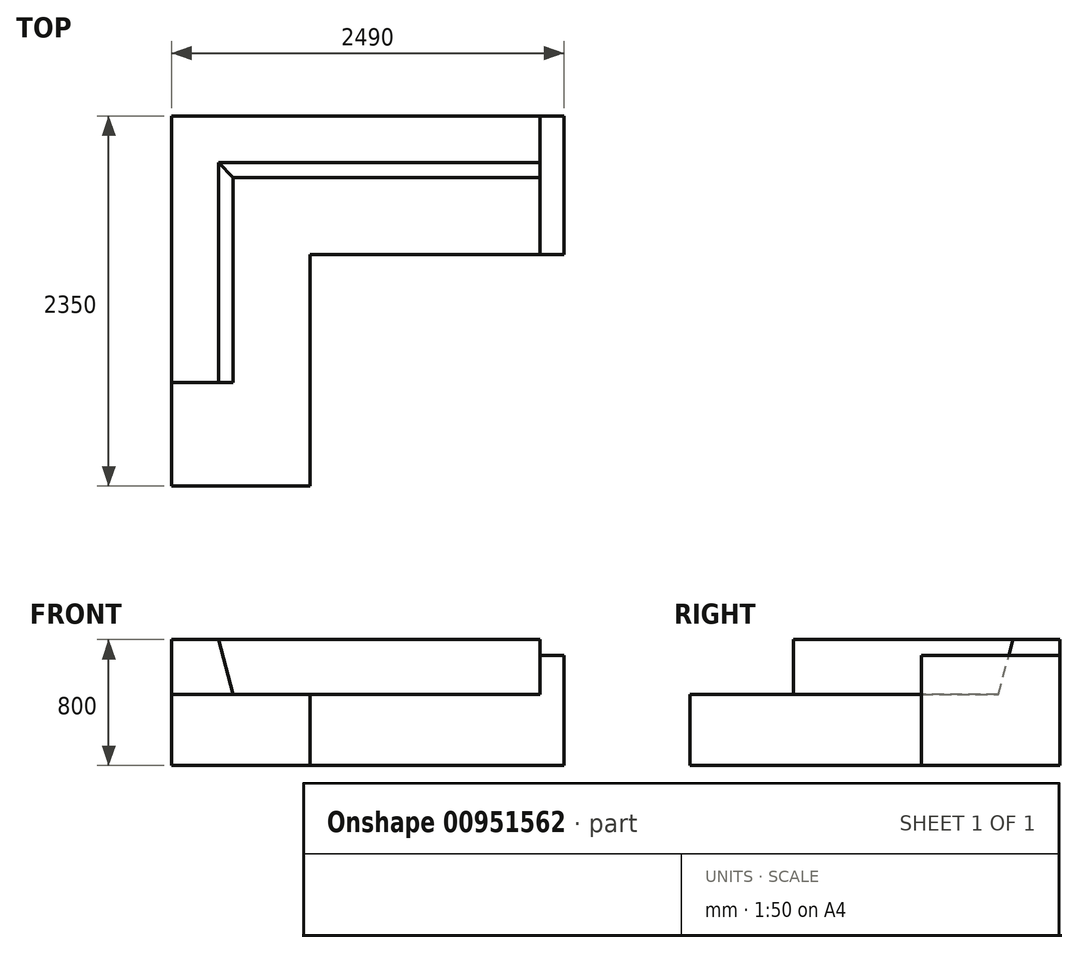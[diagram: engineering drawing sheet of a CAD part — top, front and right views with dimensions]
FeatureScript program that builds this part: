
annotation { "Feature Type Name" : "Feature", "Feature Type Description" : "" }
export const myFeature = defineFeature(function(context is Context, id is Id, definition is map)
    precondition{}
    {
        {
            var Q0;
            Q0=qCreatedBy(makeId("Top.planeOp"),FACE);
            var sketch = newSketch(context, id + "F0", { "sketchPlane" : qUnion([Q0])});
            skLineSegment(sketch, "E0", {"start": v(0, 0) * mm, "end": v(0, 2350) * mm});
            skLineSegment(sketch, "E1", {"start": v(0, 2350) * mm, "end": v(2490, 2350) * mm});
            skLineSegment(sketch, "E2", {"start": v(0, 0) * mm, "end": v(879.48, 0) * mm});
            skLineSegment(sketch, "E3", {"start": v(2490, 2350) * mm, "end": v(2490, 1470.52) * mm});
            skLineSegment(sketch, "E4", {"start": v(879.48, 0) * mm, "end": v(879.48, 1470.52) * mm});
            skLineSegment(sketch, "E5", {"start": v(879.48, 1470.52) * mm, "end": v(2490, 1470.52) * mm});
            skSolve(sketch);
        }
        {
            var Q0;
            Q0=qSketchRegion(id+"F0",true);
            extrude(context, id + "F1", {"entities" : qUnion([Q0]), "depth" : 450 * mm, "offsetDistance" : 25.4 * mm});
        }
        {
            var Q0;
            Q0=makeQuery(id+"F1.opExtrude","CAP_FACE",FACE,{"disambiguationData":[OSD([sQuery(id+"F0.wireOp",EDGE,"E0"),sQuery(id+"F0.wireOp",EDGE,"E1"),sQuery(id+"F0.wireOp",EDGE,"E2"),sQuery(id+"F0.wireOp",EDGE,"E3"),sQuery(id+"F0.wireOp",EDGE,"E4"),sQuery(id+"F0.wireOp",EDGE,"E5")])],"isStart":false});
            var sketch = newSketch(context, id + "F2", { "sketchPlane" : qUnion([Q0])});
            skLineSegment(sketch, "E6.bottom", {"start": v(879.48, 0) * mm, "end": v(0, 0) * mm});
            skLineSegment(sketch, "E6.top", {"start": v(879.48, 150) * mm, "end": v(0, 150) * mm});
            skLineSegment(sketch, "E6.left", {"start": v(879.48, 0) * mm, "end": v(879.48, 150) * mm});
            skLineSegment(sketch, "E6.right", {"start": v(0, 0) * mm, "end": v(0, 150) * mm});
            skLineSegment(sketch, "E7.bottom", {"start": v(2490, 1470.52) * mm, "end": v(2340, 1470.52) * mm});
            skLineSegment(sketch, "E7.top", {"start": v(2490, 2350) * mm, "end": v(2340, 2350) * mm});
            skLineSegment(sketch, "E7.left", {"start": v(2490, 1470.52) * mm, "end": v(2490, 2350) * mm});
            skLineSegment(sketch, "E7.right", {"start": v(2340, 1470.52) * mm, "end": v(2340, 2350) * mm});
            skSolve(sketch);
        }
        {
            var Q0;
            Q0=qSketchRegion(id+"F2",true);
            extrude(context, id + "F3", {"entities" : qUnion([Q0]), "operationType" : NewBodyOperationType.ADD, "depth" : 700 * mm - 450 * mm, "offsetDistance" : 25.4 * mm});
        }
        {
            var Q0;
            Q0=makeQuery(id+"F3.opExtrude","SWEPT_FACE",FACE,{"disambiguationData":[OSD([sQuery(id+"F2.wireOp",EDGE,"E6.top")])]});
            var sketch = newSketch(context, id + "F4", { "sketchPlane" : qUnion([Q0])});
            skLineSegment(sketch, "E8", {"start": v(0, 450) * mm, "end": v(0, 800) * mm});
            skLineSegment(sketch, "E9", {"start": v(0, 800) * mm, "end": v(-296.74, 800) * mm});
            skLineSegment(sketch, "E10", {"start": v(-296.74, 800) * mm, "end": v(-390.52, 450) * mm});
            skLineSegment(sketch, "E11", {"start": v(-390.52, 450) * mm, "end": v(0, 450) * mm});
            skSolve(sketch);
        }
        {
            var Q0;
            Q0=qSketchRegion(id+"F4",true);
            var Q1;
            Q1=makeQuery(id+"F3.boolean.opBoolean","MERGE",FACE,{"derivedFrom":[makeQuery(id+"F1.opExtrude","SWEPT_FACE",FACE,{"disambiguationData":[OSD([sQuery(id+"F0.wireOp",EDGE,"E1")])]}),makeQuery(id+"F3.opExtrude","SWEPT_FACE",FACE,{"disambiguationData":[OSD([sQuery(id+"F2.wireOp",EDGE,"E7.top")])]})]});
            extrude(context, id + "F5", {"entities" : qUnion([Q0]), "operationType" : NewBodyOperationType.ADD, "endBound" : BoundingType.UP_TO_SURFACE, "depth" : 25.4 * mm, "endBoundEntityFace" : qUnion([Q1]), "offsetDistance" : 25.4 * mm});
        }
        {
            var Q0;
            Q0=makeQuery(id+"F3.opExtrude","SWEPT_FACE",FACE,{"disambiguationData":[OSD([sQuery(id+"F2.wireOp",EDGE,"E7.right")])]});
            var sketch = newSketch(context, id + "F6", { "sketchPlane" : qUnion([Q0])});
            skLineSegment(sketch, "E12", {"start": v(-2350, 450) * mm, "end": v(-1959.47, 450) * mm});
            skLineSegment(sketch, "E13", {"start": v(-1959.47, 450) * mm, "end": v(-2053.26, 800) * mm});
            skLineSegment(sketch, "E14", {"start": v(-2053.26, 800) * mm, "end": v(-2350, 800) * mm});
            skLineSegment(sketch, "E15", {"start": v(-2350, 800) * mm, "end": v(-2350, 450) * mm});
            skSolve(sketch);
        }
        {
            var Q0;
            Q0=qSketchRegion(id+"F6",true);
            extrude(context, id + "F7", {"entities" : qUnion([Q0]), "operationType" : NewBodyOperationType.ADD, "endBound" : BoundingType.UP_TO_NEXT, "depth" : 25.4 * mm, "offsetDistance" : 25.4 * mm});
        }
        {
            var Q0;
            Q0=makeQuery(id+"F3.boolean.opBoolean","MERGE",FACE,{"derivedFrom":[makeQuery(id+"F1.opExtrude","SWEPT_FACE",FACE,{"disambiguationData":[OSD([sQuery(id+"F0.wireOp",EDGE,"E4")])]}),makeQuery(id+"F3.opExtrude","SWEPT_FACE",FACE,{"disambiguationData":[OSD([sQuery(id+"F2.wireOp",EDGE,"E6.left")])]})]});
            var sketch = newSketch(context, id + "F8", { "sketchPlane" : qUnion([Q0])});
            skLineSegment(sketch, "E16.bottom", {"start": v(658.57, 450) * mm, "end": v(0, 450) * mm});
            skLineSegment(sketch, "E16.top", {"start": v(658.57, 800) * mm, "end": v(0, 800) * mm});
            skLineSegment(sketch, "E16.left", {"start": v(658.57, 450) * mm, "end": v(658.57, 800) * mm});
            skLineSegment(sketch, "E16.right", {"start": v(0, 450) * mm, "end": v(0, 800) * mm});
            skSolve(sketch);
        }
        {
            var Q0;
            Q0 = qSketchRegion(id + "F8", true);
            extrude(context, id + "F9", {"entities" : qUnion([Q0]), "operationType" : NewBodyOperationType.REMOVE, "endBound" : BoundingType.THROUGH_ALL, "oppositeDirection" : true, "depth" : 25.4 * mm, "offsetDistance" : 25.4 * mm});
        }
    });
